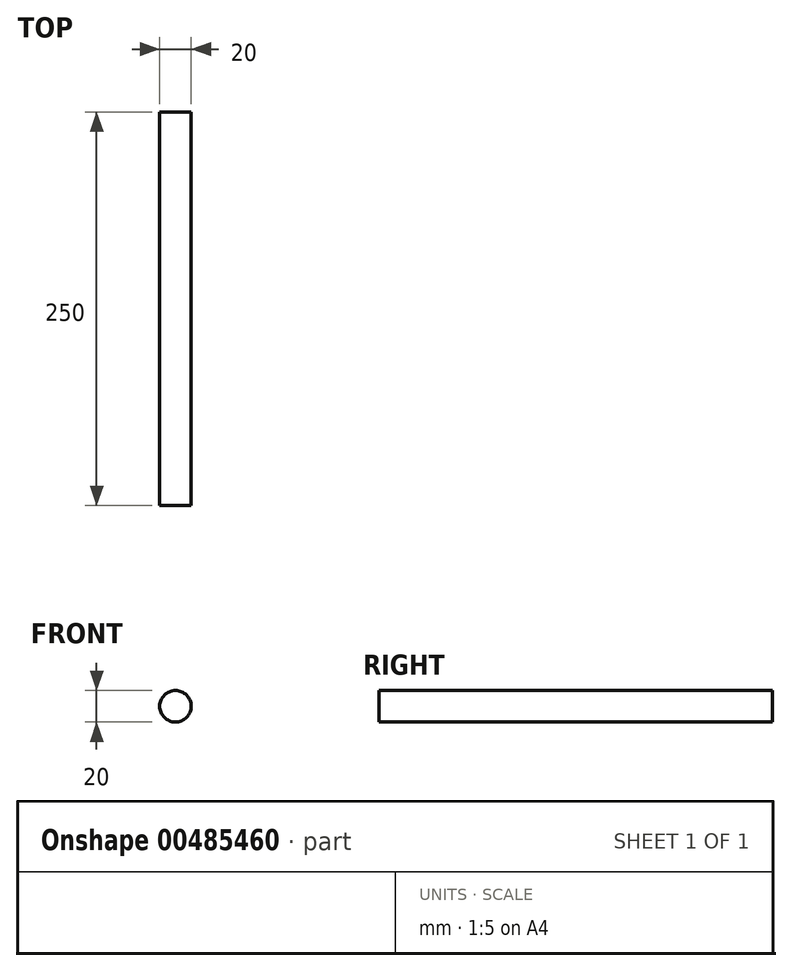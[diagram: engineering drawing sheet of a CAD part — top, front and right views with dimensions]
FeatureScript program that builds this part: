
annotation { "Feature Type Name" : "Feature", "Feature Type Description" : "" }
export const myFeature = defineFeature(function(context is Context, id is Id, definition is map)
    precondition{}
    {
        {
            var Q0;
            Q0=qCreatedBy(makeId("Front.planeOp"),FACE);
            var sketch = newSketch(context, id + "F0", { "sketchPlane" : qUnion([Q0])});
            skCircle(sketch, "E0", {"center": v(21.34, 16.24) * mm, "radius": 10 * mm});
            skSolve(sketch);
        }
        {
            var Q0;
            Q0=makeQuery(id+"F0.imprint","IMPRINT",FACE,{"disambiguationData":[TD([[makeQuery(id+"F0.imprint","IMPRINT",EDGE,{"derivedFrom":sQuery(id+"F0.wireOp",EDGE,"E0")}),1.0]])]});
            extrude(context, id + "F1", {"entities" : qUnion([Q0]), "depth" : 250 * mm});
        }
    });
